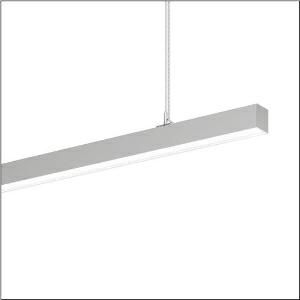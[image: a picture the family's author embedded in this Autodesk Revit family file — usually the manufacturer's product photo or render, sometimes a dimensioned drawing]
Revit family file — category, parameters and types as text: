
# Revit family: silica_r__21_51mx30tct9s_9c67
name_source: partatom
category: Lighting Fixtures
units: mm (PartAtom-declared; Revit-internal decimal feet)

## family parameters
Cut with Voids When Loaded = No
Host = Face
Light Source = No
Part Type = Normal
Room Calculation Point = No
Round Connector Dimension = Use Diameter
Shared = No

## types (1)
- --- (1 x LED, 10300 lm, 84.4 W, 6500K)
    Apparent Load = 84 VA
    CIE Flux Codes = 47 79 96 58 100
    Color Rendering = 80
    Color Temperature = 6500K
    Default Elevation = 1800 mm
    Description = Silica® 21, office luminaire, primary optical cover: cover, of PMMA, opal, light emission: direct/indirect distribution, primary light characteristic: symmetric, installation type: suspended mounting, LED, rated luminous flux: 10.300lm, luminous efficacy: 116lm/W, light colour: 8tw, colour temperature: 2700..6500K, control gear: ECG DALI, with terminal, 3+2-pole, max. 2.5mm², mains connection: 220..240V, AC, 50/60Hz, rated input power: 88.7W, luminaire housing, of aluminium, metallic grey (RAL 9006), length: 3.004mm, width: 53mm, height: 53mm, protection rating (complete): IP20, insulation class (complete): insulation class I (protective earthing), certification: CE, permissible operating ambient temperature: 0..+35°C, standard: EN 50419, packaging unit: 1 piece
    Height = 53 mm
    Lamp = 1 x LED
    Lamp Light Flux = 10300 lm
    Lamp Power = 84.4 W
    Lamp count = 1
    Length = 3004 mm
    Luminous efficacy = 122 lm/W
    Manufacturer = Siteco
    ModVariant = No
    Model = 51MX30TCT9S
    Mounting Place = Ceiling
    Mounting Type = Pendant
    Number of Poles = 1
    OnlyDefault = Yes
    Power Factor = 1
    Product Name = Silica® 21
    Product group = office luminaire | ceiling pendant
    ProductGroupID = 902
    Protection Class = Protection class I
    Protection Degree = IP 20
    RLX_Detail_Level = 1
    RLX_Emergency_Light_Flux = 0 lm
    RLX_Emergency_Type = 0
    RLX_Emergency_Type_DB = No
    RlxData = <blob elided: 20061 chars, md5=9bdada5f>
    Socket = socket
    Standby Power = 0 W
    System Light Flux = 10300 lm
    System Power = 84 W
    Type Comments = individual setting
    Type Image = l_1313621.jpg
    URL = http://relux.com
    VarID = @adj_088977
    Voltage = 0 V
    Weight = 0.00 kg
    Width = 53 mm

## geometry (parser evidence)
native form markers: Blend x4, Sweep x13
no freeform markers — native parametric forms only
